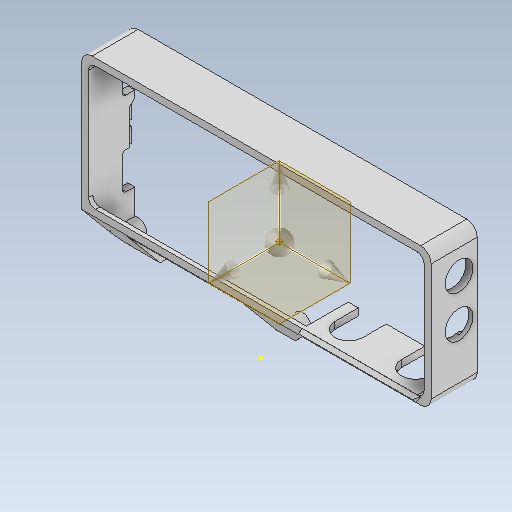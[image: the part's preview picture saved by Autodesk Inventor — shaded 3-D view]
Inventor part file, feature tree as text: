
AUTODESK INVENTOR PART (.ipt)
format: ipt  version: 2021 (Build 250183000, 183)  size: 623,104 bytes
history: native  units: mm
features: sketch x28, extrude x26, fillet x6, chamfer x6, hole x1
ambient origin geometry x8: Origin, YZ Plane, XZ Plane, XY Plane, X Axis, Y Axis, Z Axis, Center Point
bodies: Solid1 (feature_tree)
feature tree (67):
  extrude  "Extrusion1"  Depth=100.0mm
  extrude  "Extrusion3"  Depth=50.0mm
  extrude  "Extrusion4"  Depth=12.5mm
  extrude  "Extrusion12"  Depth=3.0mm TaperAngle=0.0deg
  extrude  "Extrusion13"  Depth=3.0mm TaperAngle=0.0deg
  fillet  "Fillet3"  Radius=2.0mm
  extrude  "Extrusion15"  Depth=2.0mm
  extrude  "Extrusion20"  Depth=44.0mm
  extrude  "Extrusion21"  Depth=12.0mm TaperAngle=0.0deg
  extrude  "Extrusion22"  Depth=2.0mm
  extrude  "Extrusion23"  Depth=3.0mm
  extrude  "Extrusion26"  Depth=4.4mm TaperAngle=0.0deg
  hole  "Hole2"  [1 undecoded]
  chamfer  "Chamfer5"  Distance=12.0mm
  chamfer  "Chamfer7"  Distance=12.0mm
  extrude  "Extrusion27"  Depth=8.0mm
  fillet  "Fillet4"  Radius=8.0mm
  extrude  "Extrusion28"  Depth=2.0mm TaperAngle=0.0deg
  extrude  "Extrusion29"  Depth=10.0mm
  extrude  "Extrusion30"  Depth=8.0mm
  fillet  "Fillet5"  Radius=8.0mm
  extrude  "Extrusion34"  Depth=2.0mm TaperAngle=0.0deg
  extrude  "Extrusion35"  Depth=3.0mm
  extrude  "Extrusion36"  Depth=50.0mm
  extrude  "Extrusion37"  Depth=15.0mm
  fillet  "Fillet6"  Radius=3.0mm
  extrude  "Extrusion38"  Depth=97.0mm
  extrude  "Extrusion39"  Depth=4.8mm
  chamfer  "Chamfer8"  Distance=5.0mm
  extrude  "Extrusion40"  Depth=2.0mm TaperAngle=45.0deg
  fillet  "Fillet7"  Radius=68.0mm
  extrude  "Extrusion41"  Depth=2.0mm TaperAngle=0.0deg
  chamfer  "Chamfer9"  Distance=2.0mm
  chamfer  "Chamfer10"  Distance=2.0mm
  extrude  "Extrusion42"  Depth=24.0mm
  extrude  "Extrusion43"  Depth=2.0mm TaperAngle=0.0deg
  chamfer  "Chamfer11"  Distance=36.5mm
  extrude  "Extrusion44"  Depth=46.5mm
  fillet  "Fillet8"  Radius=3.5mm
  sketch  "Sketch49"  dims[d180=0.8mm d181=2.0mm d182=45.0deg d184=68.0mm d189=2.0mm d190=0.0mm d191=2.0mm d192=2.0mm d193=24.0mm d194=2.0mm d195=0.0mm d196=36.5mm d197=46.5mm d198=3.5mm d199=2.0mm d200=0.0mm d201=12.5mm d202=23.0mm d203=3.5mm d204=2.0mm d205=0.0mm d206=1.0mm d217=7.6mm d218=10.0mm d219=46.4mm d220=20.0mm d221=0.0mm d222=22.68928mm d223=67.0mm d224=0.0mm d225=1.2mm d226=0.0mm d227=1.2mm d228=0.0mm d229=3.0mm d230=12.3mm d231=33.2mm d232=1.0mm d233=10.0mm d234=1.2mm d235=0.0mm d236=1.2mm d237=5.0mm d238=20.0mm d239=1.5mm d240=0.0mm d241=1.5mm d242=2.0mm d243=45.0deg d245=2.711255mm d246=12.0mm d247=33.2mm d248=3.0mm d249=0.0mm d251=2.0mm d252=1.2mm d253=10.0mm d254=1.5mm d255=0.0mm d256=1.5mm d257=2.0mm d258=45.0deg d259=3.35mm d260=2.0mm d261=45.0deg d262=1.6mm d263=2.0mm d264=0.0mm d265=2.0mm d266=0.0mm d267=1.3mm d268=2.0mm d269=45.0deg d270=2.0mm d271=2.0mm d272=1.2mm d273=0.0mm d274=2.0mm d67=0.5mm d68=0.872665mm d69=0.5mm d70=0.872665mm d71=0.5mm d72=0.872665mm d73=0.5mm d74=0.872665mm d75=0.872665mm d76=0.5mm d77=0.872665mm d208=0.5mm d209=0.872665mm d210=0.5mm d211=0.872665mm]
  sketch  "Sketch1"  dims[d0=52.0mm d1=100.0mm]
  sketch  "Sketch4"  dims[d2=26.0mm d3=50.0mm]
  sketch  "Sketch5"  dims[d4=1.2mm d5=0.0mm d35=12.5mm]
  sketch  "Sketch13"  dims[d36=63.1mm d37=3.0mm d38=0.0mm]
  sketch  "Sketch14"  dims[d39=50.673mm d40=3.0mm d41=0.0mm d79=2.0mm]
  sketch  "Sketch16"  dims[d80=2.0mm d81=2.0mm]
  sketch  "Sketch21"  dims[d82=1.2mm d83=44.0mm]
  sketch  "Sketch22"  dims[d84=59.0mm d85=12.0mm d86=0.0mm]
  sketch  "Sketch23"  dims[d87=2.0mm d88=12.6mm]
  sketch  "Sketch24"  dims[d89=12.0mm d90=0.0mm d91=3.0mm]
  sketch  "Sketch27"  dims[d95=33.8mm d96=4.4mm d97=0.0mm]
  sketch  "Sketch28"  dims[d117=2.0mm d118=2.0mm d119=12.0mm d120=0.0mm d121=12.0mm d122=0.0mm]
  sketch  "Sketch29"  dims[d123=70.0mm d124=89.0mm d125=8.0mm]
  sketch  "Sketch30"  dims[d126=8.0mm d127=2.0mm d128=0.0mm]
  sketch  "Sketch31"  dims[d129=8.0mm d130=10.0mm]
  sketch  "Sketch32"  dims[d131=12.0mm d132=8.0mm d133=8.0mm]
  sketch  "Sketch36"  dims[d134=8.0mm d135=2.0mm d136=0.0mm]
  sketch  "Sketch37"  dims[d144=3.0mm d145=3.0mm]
  sketch  "Sketch38"  dims[d146=3.0mm d147=50.0mm]
  sketch  "Sketch39"  dims[d148=97.0mm d149=15.0mm d150=3.0mm]
  sketch  "Sketch40"  dims[d151=3.0mm d152=97.0mm]
  sketch  "Sketch41"  dims[d153=49.0mm d154=4.8mm]
  sketch  "Sketch43"  dims[d155=4.8mm]
  sketch  "Sketch45"  dims[d156=4.8mm]
  sketch  "Sketch46"  dims[d157=4.8mm]
  sketch  "Sketch47"  dims[d158=4.8mm d159=5.0mm d160=0.0mm]
  sketch  "Sketch48"  dims[d161=2.0mm d162=6.0mm d163=4.0mm d164=2.0mm d165=90.0deg d166=4.0mm d167=20.594885mm d174=2.0mm d175=2.0mm d176=45.0deg]
note: 1 required parameter value undecoded (feature->parameter linkage not recoverable at this tier; creation-order binding heuristic only, values carry confidence <= 0.55)
